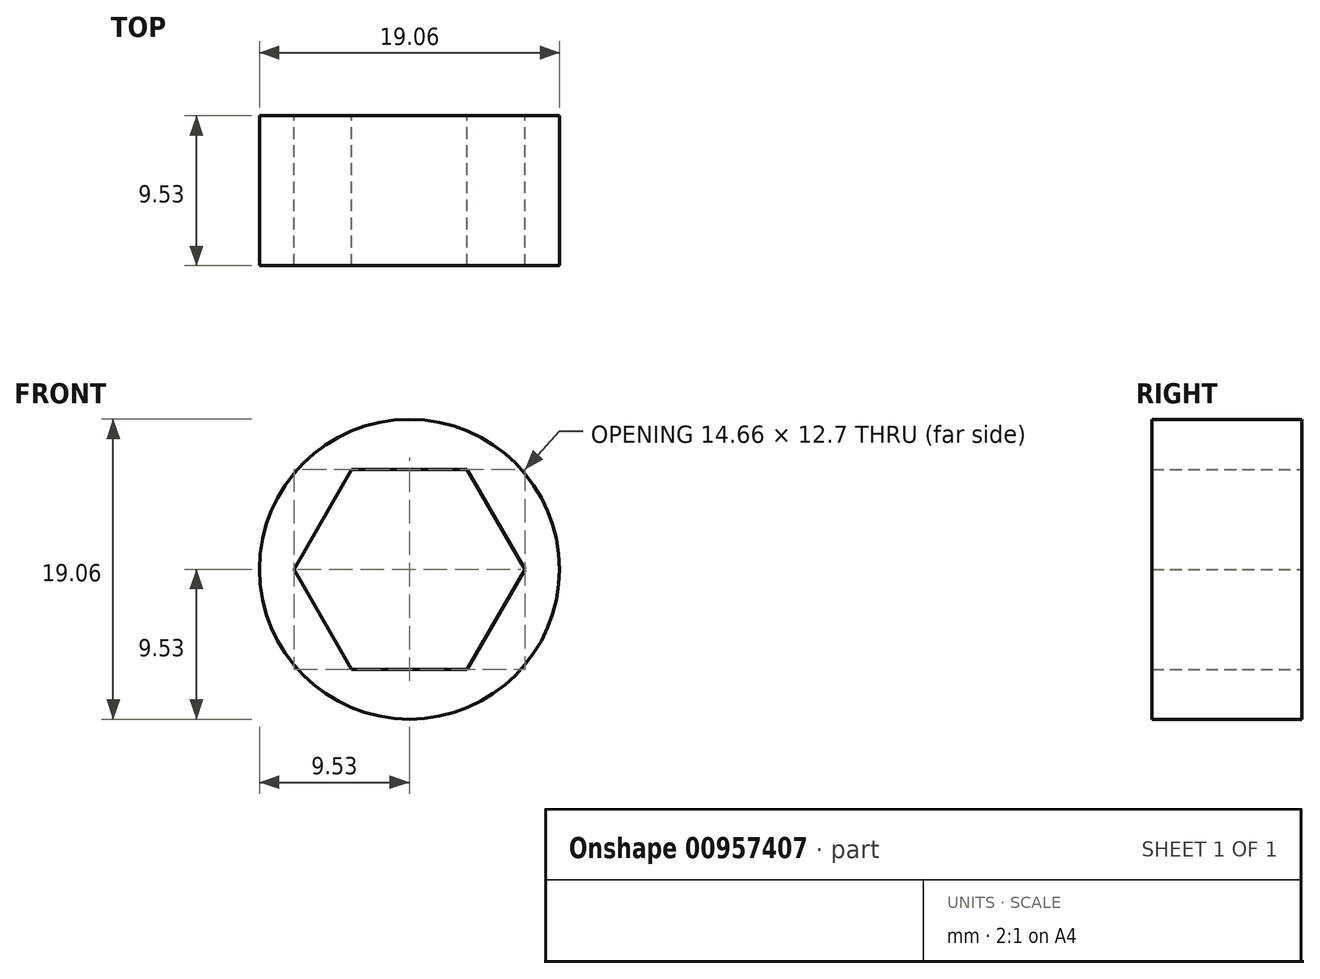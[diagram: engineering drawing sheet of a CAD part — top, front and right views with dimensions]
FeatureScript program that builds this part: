
annotation { "Feature Type Name" : "Feature", "Feature Type Description" : "" }
export const myFeature = defineFeature(function(context is Context, id is Id, definition is map)
    precondition{}
    {
        {
            var Q0;
            Q0=qCreatedBy(makeId("Front.planeOp"),FACE);
            var sketch = newSketch(context, id + "F0", { "sketchPlane" : qUnion([Q0])});
            skCircle(sketch, "E0", {"center": v(0, 0) * mm, "radius": 9.52 * mm});
            skCircle(sketch, "E1.cCircle", {"center": v(0, 0) * mm, "radius": 6.35 * mm, "construction": true});
            skLineSegment(sketch, "E1.0", {"start": v(3.67, -6.35) * mm, "end": v(-3.67, -6.35) * mm});
            skLineSegment(sketch, "E1.1", {"start": v(-3.67, -6.35) * mm, "end": v(-7.33, 0) * mm});
            skLineSegment(sketch, "E1.2", {"start": v(-7.33, 0) * mm, "end": v(-3.67, 6.35) * mm});
            skLineSegment(sketch, "E1.3", {"start": v(-3.67, 6.35) * mm, "end": v(3.67, 6.35) * mm});
            skLineSegment(sketch, "E1.4", {"start": v(3.67, 6.35) * mm, "end": v(7.33, 0) * mm});
            skLineSegment(sketch, "E1.5", {"start": v(7.33, 0) * mm, "end": v(3.67, -6.35) * mm});
            skPoint(sketch, "E1.0.midPoint", {"position": v(0, -6.35) * mm});
            skSolve(sketch);
        }
        {
            var Q0;
            Q0 = qSketchRegion(id + "F0", true);
            extrude(context, id + "F1", {"entities" : qUnion([Q0]), "depth" : 9.52 * mm, "offsetDistance" : 25.4 * mm});
        }
    });
